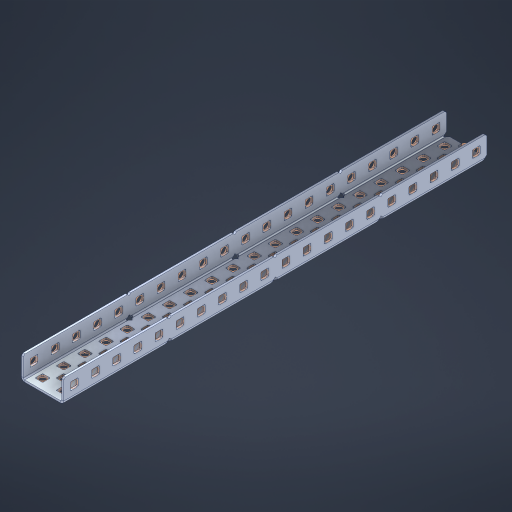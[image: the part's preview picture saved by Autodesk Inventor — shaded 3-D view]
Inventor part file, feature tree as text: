
AUTODESK INVENTOR PART (.ipt)
format: ipt  version: 2023 (Build 270158000, 158)  size: 1,409,536 bytes
history: native  units: in
note: dims shown in document units (in); Inventor stores cm internally (conversion verified against a paired STEP export)
features: other x107, extrude x98, sheet_metal_op x11, sketch x10, pattern_linear x2, mirror x1, chamfer x1
ambient origin geometry x8: Origin, YZ Plane, XZ Plane, XY Plane, X Axis, Y Axis, Z Axis, Center Point
bodies: Solid1 (feature_tree), Body (feature_tree)
feature tree (230):
  sheet_metal_op  "Flanges"
  other  "Flange Pattern Plane"
  other  "Flange Pattern Sketch"
  sheet_metal_op  "Flange Pattern"
  sheet_metal_op  "Body Pattern"
  pattern_linear  "Center Pattern"  Spacing1=0.0469in  [1 undecoded]
  other  "Arc Length"
  mirror  "Notch Mirror"
  pattern_linear  "Notch Pattern"  Spacing1=0.182in  [1 undecoded]
  chamfer  "End Chamfer"
  extrude  "Half Cut"  Depth=0.02in
  sketch  "Sketch1"  dims[d0=1.0in]
  other  "Plate1"
  sketch  "Sketch2"  dims[d1=10.0in]
  other  "Plate2"
  sheet_metal_op  "Bend1"
  sheet_metal_op  "Corner1"
  sketch  "Sketch3"  dims[d2=0.0469in]
  sketch  "Sketch7"  dims[d3=0.0469in]
  other  "Srf1"
  other  "Srf2"
  sketch  "Sketch8"  dims[d4=0.0234in]
  sketch  "Sketch9"  dims[d5=0.0938in]
  other  "Srf91"
  sheet_metal_op  "Body Pattern Sketch"
  other  "Srf92"
  sketch  "Sketch13"  dims[d6=0.0469in]
  sketch  "Sketch14"  dims[d7=0.5in d8=90.0deg d9=0.0312in]
  sketch  "Sketch15"  dims[d10=0.1875in]
  sketch  "Sketch16"  dims[d11=0.0469in d12=0.0469in d16=0.182in d17=0.02in d18=0.0469in d19=0.0in d20=0.25in d21=0.25in d38=7.874in d40=0.5in d41=0.7874in d43=1.0in d46=0.172in d47=1.0in d48=0.0in d49=0.182in d50=0.02in d51=0.25in d52=0.25in d53=0.0469in d54=0.0in d55=0.172in d56=1.0in d57=0.0in d58=0.25in d60=7.874in d62=0.5in d63=0.7874in d65=0.5in d85=0.1227in d86=0.1659in d88=0.04in d89=0.0469in d90=0.0in d91=0.04in d92=0.0491in d95=2.5in d96=0.04in d97=0.25in d98=45.0deg d99=0.25in d100=0.5in d101=0.0in d102=2.497in d106=0.182in d107=0.02in d108=0.5in d109=0.5in d110=0.0469in d111=0.0in d112=0.172in d113=0.5in d114=0.0in d117=0.5in d118=0.5in d119=0.5in]
  other  "Srf786"
  other  "Srf823"
  other  "Srf824"
  other  "Srf825"
  other  "Srf826"
  other  "Srf827"
  other  "Srf828"
  other  "Srf829"
  other  "Srf856"
  other  "Srf857"
  other  "Srf858"
  other  "Srf859"
  other  "Srf860"
  other  "Srf861"
  other  "Srf862"
  other  "Srf889"
  other  "Srf890"
  other  "Srf891"
  other  "Srf892"
  other  "Srf893"
  other  "Srf894"
  other  "Srf895"
  other  "Srf896"
  other  "Srf922"
  other  "Srf923"
  other  "Srf924"
  other  "Srf925"
  other  "Srf926"
  other  "Srf959"
  other  "Srf960"
  other  "Srf961"
  other  "Srf962"
  other  "Srf963"
  other  "Srf996"
  other  "Srf997"
  other  "Srf998"
  other  "Srf999"
  other  "Srf1000"
  other  "Srf1143"
  other  "Srf1144"
  other  "Srf1145"
  other  "Srf1146"
  other  "Srf1147"
  other  "Srf1148"
  other  "Srf1149"
  other  "Srf1150"
  other  "Srf1151"
  other  "Srf1152"
  other  "Srf1153"
  other  "Srf1154"
  other  "Srf1155"
  other  "Srf1156"
  other  "Srf1157"
  other  "Srf1158"
  other  "Srf1159"
  other  "Srf1160"
  other  "Srf1161"
  other  "Srf1162"
  other  "Srf1163"
  other  "Srf1164"
  other  "Srf1165"
  other  "Srf1166"
  other  "Srf1167"
  other  "Srf1168"
  other  "Srf1199"
  other  "Srf1200"
  other  "Srf1201"
  other  "Srf1202"
  other  "Srf1203"
  other  "Srf1204"
  other  "Srf1205"
  other  "Srf1206"
  other  "Srf1207"
  other  "Srf1208"
  other  "Srf1209"
  other  "Srf1210"
  other  "Srf1211"
  other  "Srf1212"
  other  "Srf1213"
  other  "Srf1214"
  other  "Srf1215"
  other  "Srf1216"
  other  "Srf1217"
  other  "Srf1218"
  other  "Srf1219"
  other  "Srf1220"
  other  "Srf1221"
  other  "Srf1222"
  other  "Srf1223"
  other  "Srf1224"
  other  "Srf1255"
  other  "Srf1256"
  other  "Srf1257"
  other  "Srf1258"
  other  "Srf1259"
  other  "Srf1260"
  sheet_metal_op  "Flange Stamp"
  sheet_metal_op  "Flange Circle"
  sheet_metal_op  "Body Stamp"
  sheet_metal_op  "Body Circle"
  other  "Center Stamp"
  other  "Center Circle"
  sheet_metal_op  "Notch"
  extrude  "ExtrusionSrf2"  Depth=0.0469in
  extrude  "ExtrusionSrf92"  TaperAngle=0.0deg  [1 undecoded]
  extrude  "ExtrusionSrf823"  Depth=0.5in
  extrude  "ExtrusionSrf824"  Depth=0.5in
  extrude  "ExtrusionSrf825"  Depth=0.5in
  extrude  "ExtrusionSrf826"  Depth=0.5in
  extrude  "ExtrusionSrf827"  Depth=1.0in TaperAngle=0.0deg
  extrude  "ExtrusionSrf828"  Depth=0.5in
  extrude  "ExtrusionSrf829"  Depth=0.02in
  extrude  "ExtrusionSrf856"  Depth=0.5in
  extrude  "ExtrusionSrf857"  Depth=0.5in
  extrude  "ExtrusionSrf858"  Depth=0.0469in
  extrude  "ExtrusionSrf859"  TaperAngle=0.0deg  [1 undecoded]
  extrude  "ExtrusionSrf860"  Depth=0.5in
  extrude  "ExtrusionSrf861"  Depth=1.0in TaperAngle=0.0deg
  extrude  "ExtrusionSrf862"  Depth=0.5in
  extrude  "ExtrusionSrf889"  Depth=0.5in
  extrude  "ExtrusionSrf890"  Depth=0.5in
  extrude  "ExtrusionSrf891"  Depth=0.5in
  extrude  "ExtrusionSrf892"  Depth=0.5in
  extrude  "ExtrusionSrf893"  Depth=0.5in
  extrude  "ExtrusionSrf894"  Depth=0.0469in
  extrude  "ExtrusionSrf895"  TaperAngle=0.0deg  [1 undecoded]
  extrude  "ExtrusionSrf896"  Depth=0.5in
  extrude  "ExtrusionSrf922"  Depth=0.5in
  extrude  "ExtrusionSrf923"  Depth=2.5in
  extrude  "ExtrusionSrf924"  Depth=0.5in TaperAngle=45.0deg
  extrude  "ExtrusionSrf925"  Depth=0.5in
  extrude  "ExtrusionSrf926"  Depth=0.5in TaperAngle=0.0deg
  extrude  "ExtrusionSrf959"  Depth=0.5in
  extrude  "ExtrusionSrf960"  Depth=0.5in
  extrude  "ExtrusionSrf961"  Depth=0.02in
  extrude  "ExtrusionSrf962"  Depth=0.5in
  extrude  "ExtrusionSrf963"  Depth=0.5in
  extrude  "ExtrusionSrf996"  Depth=0.0469in
  extrude  "ExtrusionSrf997"  TaperAngle=0.0deg  [1 undecoded]
  extrude  "ExtrusionSrf998"  Depth=0.5in
  extrude  "ExtrusionSrf999"  Depth=0.5in TaperAngle=0.0deg
  extrude  "ExtrusionSrf1000"  Depth=0.5in
  extrude  "ExtrusionSrf1143"  Depth=0.5in
  extrude  "ExtrusionSrf1144"  Depth=0.5in
  extrude  "ExtrusionSrf1145"  [1 undecoded]
  extrude  "ExtrusionSrf1146"  [1 undecoded]
  extrude  "ExtrusionSrf1147"  [1 undecoded]
  extrude  "ExtrusionSrf1148"  [1 undecoded]
  extrude  "ExtrusionSrf1149"  [1 undecoded]
  extrude  "ExtrusionSrf1150"  [1 undecoded]
  extrude  "ExtrusionSrf1151"  [1 undecoded]
  extrude  "ExtrusionSrf1152"  [1 undecoded]
  extrude  "ExtrusionSrf1153"  [1 undecoded]
  extrude  "ExtrusionSrf1154"  [1 undecoded]
  extrude  "ExtrusionSrf1155"  [1 undecoded]
  extrude  "ExtrusionSrf1156"  [1 undecoded]
  extrude  "ExtrusionSrf1157"  [1 undecoded]
  extrude  "ExtrusionSrf1158"  [1 undecoded]
  extrude  "ExtrusionSrf1159"  [1 undecoded]
  extrude  "ExtrusionSrf1160"  [1 undecoded]
  extrude  "ExtrusionSrf1161"  [1 undecoded]
  extrude  "ExtrusionSrf1162"  [1 undecoded]
  extrude  "ExtrusionSrf1163"  [1 undecoded]
  extrude  "ExtrusionSrf1164"  [1 undecoded]
  extrude  "ExtrusionSrf1165"  [1 undecoded]
  extrude  "ExtrusionSrf1166"  [1 undecoded]
  extrude  "ExtrusionSrf1167"  [1 undecoded]
  extrude  "ExtrusionSrf1168"  [1 undecoded]
  extrude  "ExtrusionSrf1199"  [1 undecoded]
  extrude  "ExtrusionSrf1200"  [1 undecoded]
  extrude  "ExtrusionSrf1201"  [1 undecoded]
  extrude  "ExtrusionSrf1202"  [1 undecoded]
  extrude  "ExtrusionSrf1203"  [1 undecoded]
  extrude  "ExtrusionSrf1204"  [1 undecoded]
  extrude  "ExtrusionSrf1205"  [1 undecoded]
  extrude  "ExtrusionSrf1206"  [1 undecoded]
  extrude  "ExtrusionSrf1207"  [1 undecoded]
  extrude  "ExtrusionSrf1208"  [1 undecoded]
  extrude  "ExtrusionSrf1209"  [1 undecoded]
  extrude  "ExtrusionSrf1210"  [1 undecoded]
  extrude  "ExtrusionSrf1211"  [1 undecoded]
  extrude  "ExtrusionSrf1212"  [1 undecoded]
  extrude  "ExtrusionSrf1213"  [1 undecoded]
  extrude  "ExtrusionSrf1214"  [1 undecoded]
  extrude  "ExtrusionSrf1215"  [1 undecoded]
  extrude  "ExtrusionSrf1216"  [1 undecoded]
  extrude  "ExtrusionSrf1217"  [1 undecoded]
  extrude  "ExtrusionSrf1218"  [1 undecoded]
  extrude  "ExtrusionSrf1219"  [1 undecoded]
  extrude  "ExtrusionSrf1220"  [1 undecoded]
  extrude  "ExtrusionSrf1221"  [1 undecoded]
  extrude  "ExtrusionSrf1222"  [1 undecoded]
  extrude  "ExtrusionSrf1223"  [1 undecoded]
  extrude  "ExtrusionSrf1224"  [1 undecoded]
  extrude  "ExtrusionSrf1255"  [1 undecoded]
  extrude  "ExtrusionSrf1256"  [1 undecoded]
  extrude  "ExtrusionSrf1257"  [1 undecoded]
  extrude  "ExtrusionSrf1258"  [1 undecoded]
  extrude  "ExtrusionSrf1259"  [1 undecoded]
  extrude  "ExtrusionSrf1260"  [1 undecoded]
note: 62 required parameter values undecoded (feature->parameter linkage not recoverable at this tier; creation-order binding heuristic only, values carry confidence <= 0.55)
